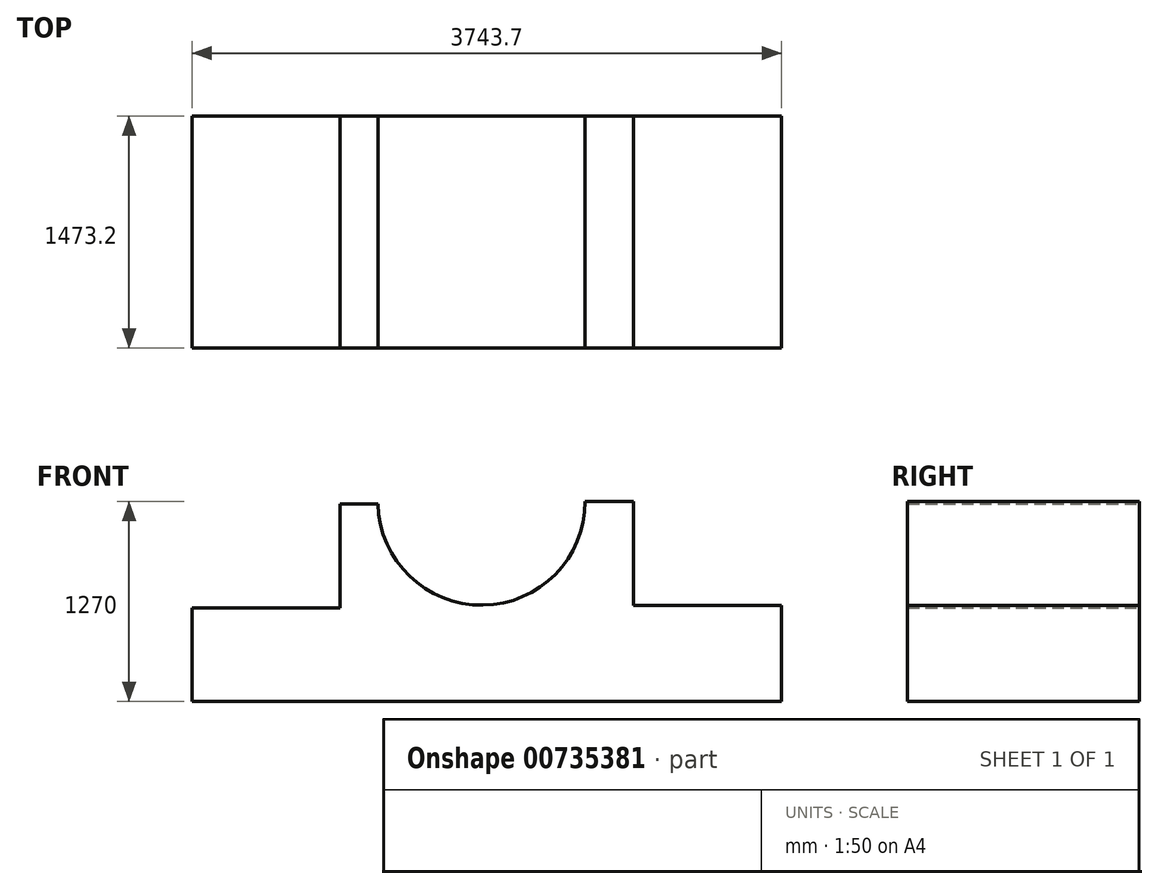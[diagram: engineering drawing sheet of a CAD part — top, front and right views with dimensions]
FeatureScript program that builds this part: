
annotation { "Feature Type Name" : "Feature", "Feature Type Description" : "" }
export const myFeature = defineFeature(function(context is Context, id is Id, definition is map)
    precondition{}
    {
        {
            var Q0;
            Q0=qCreatedBy(makeId("Front.planeOp"),FACE);
            var sketch = newSketch(context, id + "F0", { "sketchPlane" : qUnion([Q0])});
            skLineSegment(sketch, "E0", {"start": v(-66.3, 16.19) * mm, "end": v(3743.7, 16.19) * mm});
            skLineSegment(sketch, "E1", {"start": v(3743.7, 16.19) * mm, "end": v(3743.7, 625.79) * mm});
            skLineSegment(sketch, "E2", {"start": v(3743.7, 625.79) * mm, "end": v(2803.9, 625.79) * mm});
            skLineSegment(sketch, "E3", {"start": v(2803.9, 625.79) * mm, "end": v(2803.9, 1286.19) * mm});
            skLineSegment(sketch, "E4", {"start": v(2803.9, 1286.19) * mm, "end": v(2499.1, 1286.19) * mm});
            skLineSegment(sketch, "E5", {"start": v(2499.1, 1286.19) * mm, "end": v(1838.7, 1286.19) * mm});
            skLineSegment(sketch, "E6", {"start": v(0, 0) * mm, "end": v(0, 609.6) * mm});
            skLineSegment(sketch, "E7", {"start": v(0, 609.6) * mm, "end": v(939.8, 609.6) * mm});
            skLineSegment(sketch, "E8", {"start": v(939.8, 609.6) * mm, "end": v(939.8, 1270) * mm});
            skLineSegment(sketch, "E9", {"start": v(939.8, 1270) * mm, "end": v(1244.6, 1270) * mm});
            skCircle(sketch, "E10", {"center": v(1838.7, 1286.19) * mm, "radius": 658.56 * mm});
            skSolve(sketch);
        }
        {
            var Q0;
            {var subQ11=sQuery(id+"F0.wireOp",EDGE,"E1");Q0=makeQuery(id+"F0.imprint","IMPRINT",FACE,{"disambiguationData":[TD([[makeQuery(id+"F0.imprint","IMPRINT",EDGE,{"derivedFrom":subQ11}),1.0]])]});}
            extrude(context, id + "F1", {"entities" : qUnion([Q0]), "depth" : 1473.2 * mm, "offsetDistance" : 25.4 * mm});
        }
    });
